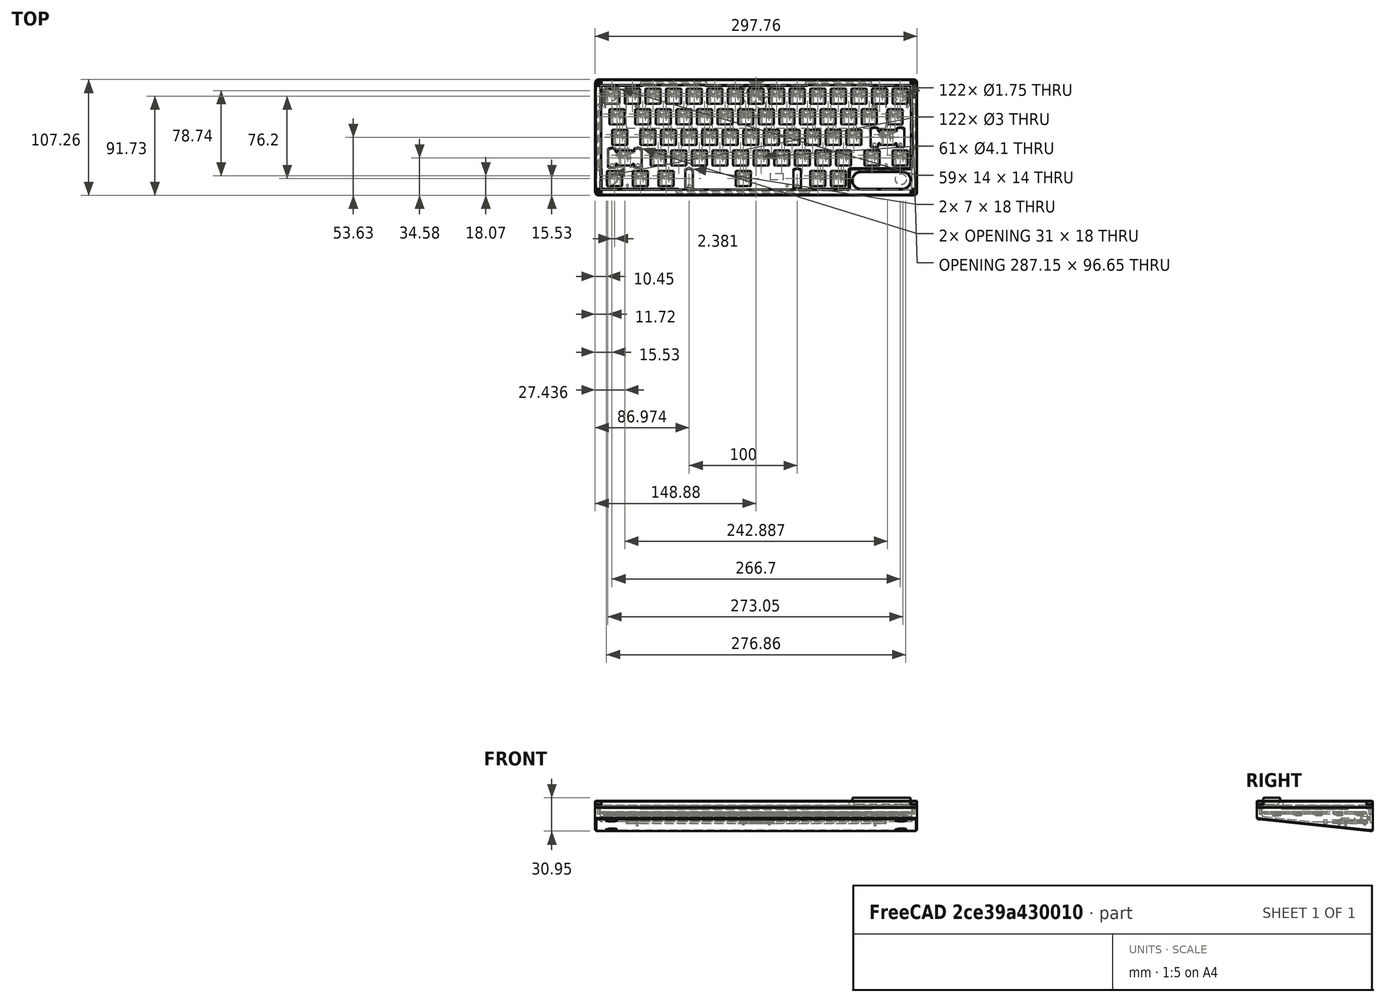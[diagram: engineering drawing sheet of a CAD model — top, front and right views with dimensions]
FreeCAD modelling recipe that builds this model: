
FCSTD DOCUMENT  (FreeCAD 0.20R29603 (Git))
Label: Five_Octave_Enclosure
License: All rights reserved
LicenseURL: http://en.wikipedia.org/wiki/All_rights_reserved
objects: Sketcher::SketchObject×21, PartDesign::Pocket×11, TechDraw::DrawViewBalloon×10, PartDesign::Fillet×9, PartDesign::Pad×6, PartDesign::Body×6, PartDesign::Chamfer×5, PartDesign::Hole×4, Part::Feature×3, PartDesign::Boolean×2, Part::MultiFuse×1, App::DocumentObjectGroup×1, TechDraw::DrawSVGTemplate×1, TechDraw::DrawViewPart×1, TechDraw::DrawPage×1
note: 103 computed .brp shape members not serialized (recipe doc carries the construction recipe); baked Part::Feature solids carry a one-line shape summary decoded from their .brp

FEATURE [Part::Feature] Feature  label="Five_Octave_MCU"
  shape: bbox 28.58 x 28.58 x 3.65 mm, 932 faces, 28 solids (baked)
FEATURE [Sketcher::SketchObject] Sketch
  AttachmentOffset = pos=(0,0,1.65) rot=(0,0,1;0rad)
  FullyConstrained = true
  MapMode = 5
  Placement = pos=(0,0,1.65) rot=(0,0,1;0rad)
  Support = -> [XY_Plane]
  expr: Constraints[12] = 15.637mm
  sketch-geometry (5):
    g0: LineSegment StartX=-4.47 StartY=15.637 StartZ=0 EndX=4.47 EndY=15.637 EndZ=0
    g1: LineSegment StartX=4.47 StartY=15.637 StartZ=0 EndX=4.47 EndY=8.337 EndZ=0
    g2: LineSegment StartX=4.47 StartY=8.337 StartZ=0 EndX=-4.47 EndY=8.337 EndZ=0
    g3: LineSegment StartX=-4.47 StartY=8.337 StartZ=0 EndX=-4.47 EndY=15.637 EndZ=0
    g4: GeomPoint X=0 Y=15.637 Z=0
  constraints (13):
    c: Coincident(g0,g1)
    c: Coincident(g1,g2)
    c: Coincident(g2,g3)
    c: Coincident(g3,g0)
    c: Horizontal(g0)
    c: Horizontal(g2)
    c: Vertical(g1)
    c: Vertical(g3)
    c: DistanceX(g0,g0) = 8.94
    c: DistanceY(g1,g1) = 7.3
    c: Symmetric(g0,g0,g4)
    c: PointOnObject(g4,g-2)
    c: DistanceY(g-1,g4) = 15.637
FEATURE [PartDesign::Pad] Pad
  Direction = (0,0,1)
  Length = 3.2
  Length2 = 10
  Profile = -> Sketch
  ReferenceAxis = -> Sketch [N_Axis]
  Type = 0
FEATURE [Sketcher::SketchObject] Sketch001
  ExternalGeometry = -> [Pad]
  FullyConstrained = true
  MapMode = 5
  Placement = pos=(0,15.637,0) rot=(0,0.707107,0.707107;3.14159rad)
  Support = -> [Pad]
  sketch-geometry (12):
    g0: ArcOfCircle CenterX=-3.22 CenterY=3.6 CenterZ=0 NormalX=0 NormalY=0 NormalZ=1 AngleXU=0 Radius=1.25 StartAngle=1.5708 EndAngle=3.14159
    g1: LineSegment StartX=-4.47 StartY=4.85 StartZ=0 EndX=-3.22 EndY=4.85 EndZ=0
    g2: LineSegment StartX=-4.47 StartY=3.6 StartZ=0 EndX=-4.47 EndY=4.85 EndZ=0
    g3: ArcOfCircle CenterX=3.22 CenterY=3.6 CenterZ=0 NormalX=0 NormalY=0 NormalZ=1 AngleXU=0 Radius=1.25 StartAngle=1e-16 EndAngle=1.5708
    g4: LineSegment StartX=3.22 StartY=4.85 StartZ=0 EndX=4.47 EndY=4.85 EndZ=0
    g5: LineSegment StartX=4.47 StartY=3.6 StartZ=0 EndX=4.47 EndY=4.85 EndZ=0
    g6: ArcOfCircle CenterX=-3.22 CenterY=2.9 CenterZ=0 NormalX=0 NormalY=0 NormalZ=1 AngleXU=0 Radius=1.25 StartAngle=3.14159 EndAngle=4.71239
    g7: LineSegment StartX=-4.47 StartY=1.65 StartZ=0 EndX=-4.47 EndY=2.9 EndZ=0
    g8: LineSegment StartX=-4.47 StartY=1.65 StartZ=0 EndX=-3.22 EndY=1.65 EndZ=0
    g9: ArcOfCircle CenterX=3.22 CenterY=2.9 CenterZ=0 NormalX=0 NormalY=0 NormalZ=1 AngleXU=0 Radius=1.25 StartAngle=4.71239 EndAngle=6.28319
    g10: LineSegment StartX=4.47 StartY=1.65 StartZ=0 EndX=3.22 EndY=1.65 EndZ=0
    g11: LineSegment StartX=4.47 StartY=1.65 StartZ=0 EndX=4.47 EndY=2.9 EndZ=0
  constraints (36):
    c: PointOnObject(g0,g-3)
    c: PointOnObject(g0,g-5)
    c: Radius(g0) = 1.25
    c: Coincident(g1,g-5)
    c: Coincident(g1,g0)
    c: DistanceX(g1,g1) = 1.25
    c: Coincident(g2,g0)
    c: Coincident(g2,g1)
    c: DistanceY(g2,g2) = 1.25
    c: PointOnObject(g3,g-3)
    c: PointOnObject(g3,g-6)
    c: Coincident(g4,g3)
    c: Coincident(g4,g-6)
    c: Coincident(g5,g4)
    c: Coincident(g5,g3)
    c: PointOnObject(g6,g-5)
    c: PointOnObject(g6,g-4)
    c: Equal(g6,g0)
    c: Equal(g3,g0)
    c: Equal(g1,g4)
    c: Equal(g5,g2)
    c: Coincident(g7,g-5)
    c: Coincident(g8,g7)
    c: Coincident(g8,g6)
    c: Coincident(g6,g7)
    c: Equal(g7,g2)
    c: Equal(g1,g8)
    c: PointOnObject(g9,g-6)
    c: PointOnObject(g9,g-4)
    c: Equal(g9,g0)
    c: Coincident(g10,g-6)
    c: Coincident(g11,g10)
    c: Coincident(g9,g11)
    c: Coincident(g10,g9)
    c: Equal(g10,g1)
    c: Equal(g11,g2)
FEATURE [PartDesign::Pocket] Pocket
  BaseFeature = -> Pad
  Direction = (0,-1,2e-16)
  Length = 7.3
  Length2 = 5
  Profile = -> Sketch001
  ReferenceAxis = -> Sketch001 [N_Axis]
  Type = 0
FEATURE [PartDesign::Body] Body  label="USB"
  Group = -> [Sketch,Pad,Sketch001,Pocket]
  Origin = -> Origin
  Tip = -> Pocket
FEATURE [Part::MultiFuse] Fusion  label="MCU"
  Placement = pos=(0,34.1625,0) rot=(0,0,1;0rad)
  Shapes = -> [Body,Feature]
  expr: .Placement.Base.y = 19.05mm * (5 - 1.5) / 2 + 1mm - 0.35mm / 2
FEATURE [Part::Feature] Feature001  label="Five_Octave_Keys"
  Placement = pos=(0,0,9.2) rot=(0,1,0;3.14159rad)
  shape: bbox 285.8 x 95.25 x 3.65 mm, 9961 faces, 246 solids (baked)
  expr: .Placement.Base.z = 3.2mm + 6mm
FEATURE [Part::Feature] Solid  label="Five_Octave_Plate"
  Placement = pos=(0,0,12.6) rot=(0,0,1;0rad)
  shape: bbox 290.8 x 100.3 x 1.6 mm, 520 faces (baked)
  expr: .Placement.Base.z = 3.2mm + 1.85mm + 3.2mm + 0.1mm + 0.85mm + 3.4mm
FEATURE [App::DocumentObjectGroup] Group  label="External Components"
  Group = -> [Fusion,Feature001,Solid]
FEATURE [Sketcher::SketchObject] Sketch002
  AttachmentOffset = pos=(0,0,-20) rot=(0,0,1;0rad)
  FullyConstrained = true
  MapMode = 5
  Placement = pos=(0,0,-20) rot=(0,0,1;0rad)
  Support = -> [XY_Plane001]
  expr: Constraints[10] = 19.05mm * 5
  expr: Constraints[19] = 5mm + 1mm
  expr: Constraints[20] = 5mm + 1mm
  expr: Constraints[9] = 19.05mm * 15
  sketch-geometry (8):
    g0: LineSegment StartX=-142.875 StartY=47.625 StartZ=0 EndX=142.875 EndY=47.625 EndZ=0
    g1: LineSegment StartX=142.875 StartY=47.625 StartZ=0 EndX=142.875 EndY=-47.625 EndZ=0
    g2: LineSegment StartX=142.875 StartY=-47.625 StartZ=0 EndX=-142.875 EndY=-47.625 EndZ=0
    g3: LineSegment StartX=-142.875 StartY=-47.625 StartZ=0 EndX=-142.875 EndY=47.625 EndZ=0
    g4: LineSegment StartX=-148.875 StartY=53.625 StartZ=0 EndX=148.875 EndY=53.625 EndZ=0
    g5: LineSegment StartX=148.875 StartY=53.625 StartZ=0 EndX=148.875 EndY=-53.625 EndZ=0
    g6: LineSegment StartX=148.875 StartY=-53.625 StartZ=0 EndX=-148.875 EndY=-53.625 EndZ=0
    g7: LineSegment StartX=-148.875 StartY=-53.625 StartZ=0 EndX=-148.875 EndY=53.625 EndZ=0
  constraints (22):
    c: Coincident(g0,g1)
    c: Coincident(g1,g2)
    c: Coincident(g2,g3)
    c: Coincident(g3,g0)
    c: Horizontal(g0)
    c: Horizontal(g2)
    c: Vertical(g1)
    c: Vertical(g3)
    c: Symmetric(g0,g1,g-1)
    c: DistanceX(g0,g0) = 285.75
    c: DistanceY(g3,g3) = 95.25
    c: Coincident(g4,g5)
    c: Coincident(g5,g6)
    c: Coincident(g6,g7)
    c: Coincident(g7,g4)
    c: Horizontal(g4)
    c: Horizontal(g6)
    c: Vertical(g5)
    c: Vertical(g7)
    c: DistanceX(g4,g0) = 6
    c: DistanceY(g0,g4) = 6
    c: Symmetric(g4,g5,g-1)
FEATURE [PartDesign::Pad] Pad001
  Direction = (0,0,1)
  Length = 33.4
  Length2 = 10
  Profile = -> Sketch002
  ReferenceAxis = -> Sketch002 [N_Axis]
  Type = 0
  expr: Length = 12.6mm + 1.6mm / 2 + 20mm
FEATURE [Sketcher::SketchObject] Sketch003
  ExternalGeometry = -> [Pad001]
  FullyConstrained = true
  MapMode = 5
  Placement = pos=(148.875,0,0) rot=(0.57735,0.57735,0.57735;2.0944rad)
  Support = -> [Pad001]
  sketch-geometry (5):
    g0: LineSegment StartX=-53.625 StartY=2.61969 StartZ=0 EndX=53.625 EndY=-8.65274 EndZ=0
    g1: LineSegment StartX=53.625 StartY=-20 StartZ=0 EndX=-53.625 EndY=-20 EndZ=0
    g2: LineSegment StartX=-53.625 StartY=-20 StartZ=0 EndX=-53.625 EndY=2.61969 EndZ=0
    g3: LineSegment StartX=53.625 StartY=-20 StartZ=0 EndX=53.625 EndY=-8.65274 EndZ=0
    g4: LineSegment StartX=0 StartY=0 StartZ=0 EndX=-0.313585 EndY=-2.98357 EndZ=0
  constraints (13):
    c: PointOnObject(g0,g-3)
    c: Coincident(g3,g-4)
    c: Coincident(g1,g3)
    c: Coincident(g1,g-3)
    c: Coincident(g2,g1)
    c: Coincident(g2,g0)
    c: Angle(g0,g-1) = 0.10472
    c: Coincident(g3,g0)
    c: PointOnObject(g0,g-4)
    c: Coincident(g4,g-1)
    c: PointOnObject(g4,g0)
    c: Perpendicular(g0,g4)
    c: Distance(g4) = 3
FEATURE [PartDesign::Pocket] Pocket001
  BaseFeature = -> Pad001
  Direction = (-1,0,0)
  Length = 310
  Length2 = 5
  Profile = -> Sketch003
  ReferenceAxis = -> Sketch003 [N_Axis]
  Type = 0
FEATURE [Sketcher::SketchObject] Sketch004
  AttachmentOffset = pos=(0,0,-20) rot=(0,0,1;0rad)
  FullyConstrained = true
  MapMode = 5
  Placement = pos=(0,0,-20) rot=(0,0,1;0rad)
  Support = -> [XY_Plane002]
  expr: .AttachmentOffset.Base.z = -20mm
  expr: Constraints[10] = 19.05mm * 15
  expr: Constraints[11] = 19.05mm * 5
  sketch-geometry (10):
    g0: LineSegment StartX=142.875 StartY=-47.625 StartZ=0 EndX=142.875 EndY=47.625 EndZ=0
    g1: LineSegment StartX=142.875 StartY=47.625 StartZ=0 EndX=-142.875 EndY=47.625 EndZ=0
    g2: LineSegment StartX=-142.875 StartY=47.625 StartZ=0 EndX=-142.875 EndY=-47.625 EndZ=0
    g3: LineSegment StartX=-142.875 StartY=-47.625 StartZ=0 EndX=142.875 EndY=-47.625 EndZ=0
    g4: GeomPoint X=0 Y=0 Z=0
    g5: LineSegment StartX=143.875 StartY=-48.625 StartZ=0 EndX=143.875 EndY=48.625 EndZ=0
    g6: LineSegment StartX=143.875 StartY=48.625 StartZ=0 EndX=-143.875 EndY=48.625 EndZ=0
    g7: LineSegment StartX=-143.875 StartY=48.625 StartZ=0 EndX=-143.875 EndY=-48.625 EndZ=0
    g8: LineSegment StartX=-143.875 StartY=-48.625 StartZ=0 EndX=143.875 EndY=-48.625 EndZ=0
    g9: GeomPoint X=0 Y=0 Z=0
  constraints (24):
    c: Coincident(g0,g1)
    c: Coincident(g1,g2)
    c: Coincident(g2,g3)
    c: Coincident(g3,g0)
    c: Horizontal(g1)
    c: Horizontal(g3)
    c: Vertical(g0)
    c: Vertical(g2)
    c: Symmetric(g1,g0,g4)
    c: Coincident(g4,g-1)
    c: DistanceX(g1,g1) = 285.75
    c: DistanceY(g2,g2) = 95.25
    c: Coincident(g5,g6)
    c: Coincident(g6,g7)
    c: Coincident(g7,g8)
    c: Coincident(g8,g5)
    c: Horizontal(g6)
    c: Horizontal(g8)
    c: Vertical(g5)
    c: Vertical(g7)
    c: Symmetric(g6,g5,g9)
    c: Coincident(g9,g4)
    c: DistanceX(g6,g1) = 1
    c: DistanceY(g1,g6) = 1
FEATURE [PartDesign::Pad] Pad002
  Direction = (0,0,1)
  Length = 33.4
  Length2 = 10
  Profile = -> Sketch004
  ReferenceAxis = -> Sketch004 [N_Axis]
  Type = 0
  expr: Length = 12.6mm + 1.6mm / 2 + 20mm
FEATURE [Sketcher::SketchObject] Sketch005
  ExternalGeometry = -> [Pad002]
  FullyConstrained = true
  MapMode = 5
  Placement = pos=(143.875,0,0) rot=(0.57735,0.57735,0.57735;2.0944rad)
  Support = -> [Pad002]
  sketch-geometry (6):
    g0: LineSegment StartX=-48.625 StartY=-20 StartZ=0 EndX=48.625 EndY=-20 EndZ=0
    g1: LineSegment StartX=-48.625 StartY=5.11069 StartZ=0 EndX=0 EndY=0 EndZ=0
    g2: LineSegment StartX=-48.625 StartY=5.11069 StartZ=0 EndX=-48.625 EndY=-20 EndZ=0
    g3: LineSegment StartX=0 StartY=0 StartZ=0 EndX=48.625 EndY=0 EndZ=0
    g4: LineSegment StartX=48.625 StartY=0 StartZ=0 EndX=48.625 EndY=-20 EndZ=0
    g5: LineSegment StartX=0 StartY=0 StartZ=0 EndX=-48.625 EndY=0 EndZ=0
  constraints (15):
    c: Coincident(g0,g-3)
    c: PointOnObject(g1,g-5)
    c: Coincident(g2,g1)
    c: Coincident(g2,g0)
    c: Coincident(g0,g-5)
    c: Coincident(g3,g1)
    c: Horizontal(g3)
    c: Coincident(g4,g3)
    c: Coincident(g4,g0)
    c: Coincident(g-1,g1)
    c: PointOnObject(g3,g-4)
    c: Coincident(g5,g1)
    c: PointOnObject(g5,g2)
    c: Horizontal(g5)
    c: Angle(g1,g5) = 0.10472
FEATURE [PartDesign::Pocket] Pocket002
  BaseFeature = -> Pad002
  Direction = (-1,0,0)
  Length = 300
  Length2 = 5
  Profile = -> Sketch005
  ReferenceAxis = -> Sketch005 [N_Axis]
  Type = 0
FEATURE [PartDesign::Body] Body002  label="Case_Pocket"
  Group = -> [Sketch004,Pad002,Sketch005,Pocket002]
  Origin = -> Origin002
  Tip = -> Pocket002
FEATURE [PartDesign::Boolean] Boolean
  BaseFeature = -> Pocket001
  Group = -> [Body002]
  Type = 1
FEATURE [PartDesign::Fillet] Fillet
  Base = -> Boolean [Edge22,Edge25,Edge19,Edge20]
  BaseFeature = -> Boolean
  Radius = 2
  SupportTransform = false
  UseAllEdges = false
FEATURE [Sketcher::SketchObject] Sketch006
  ExternalGeometry = -> [Fillet]
  FullyConstrained = true
  MapMode = 5
  Placement = pos=(0,0,13.4) rot=(0,0,1;0rad)
  Support = -> [Fillet]
  expr: Constraints[10] = 19.05mm * 2.5 - 2mm
  expr: Constraints[20] = 19.05mm * 3 + 4mm
  expr: Constraints[21] = 19.05mm * 2.5 - 2mm
  expr: Constraints[31] = 19.05mm * 3 + 4mm
  expr: Constraints[32] = 19.05mm * 1.5 + 2mm
  expr: Constraints[42] = 19.05mm * 2 + 4mm
  expr: Constraints[43] = 19.05mm * 1.5 + 2mm
  expr: Constraints[53] = 19.05mm * 6.25 + 4mm
  expr: Constraints[54] = 19.05mm * (7.5 - 1.25 * 3) + 2mm
  expr: Constraints[9] = 19.05mm * 3 + 4mm
  sketch-geometry (20):
    g0: LineSegment StartX=-106.775 StartY=51.625 StartZ=0 EndX=-45.625 EndY=51.625 EndZ=0
    g1: LineSegment StartX=-45.625 StartY=51.625 StartZ=0 EndX=-45.625 EndY=48.625 EndZ=0
    g2: LineSegment StartX=-45.625 StartY=48.625 StartZ=0 EndX=-106.775 EndY=48.625 EndZ=0
    g3: LineSegment StartX=-106.775 StartY=48.625 StartZ=0 EndX=-106.775 EndY=51.625 EndZ=0
    g4: LineSegment StartX=45.625 StartY=51.625 StartZ=0 EndX=106.775 EndY=51.625 EndZ=0
    g5: LineSegment StartX=106.775 StartY=51.625 StartZ=0 EndX=106.775 EndY=48.625 EndZ=0
    g6: LineSegment StartX=106.775 StartY=48.625 StartZ=0 EndX=45.625 EndY=48.625 EndZ=0
    g7: LineSegment StartX=45.625 StartY=48.625 StartZ=0 EndX=45.625 EndY=51.625 EndZ=0
    g8: LineSegment StartX=-146.875 StartY=30.575 StartZ=0 EndX=-143.875 EndY=30.575 EndZ=0
    g9: LineSegment StartX=-143.875 StartY=30.575 StartZ=0 EndX=-143.875 EndY=-30.575 EndZ=0
    g10: LineSegment StartX=-143.875 StartY=-30.575 StartZ=0 EndX=-146.875 EndY=-30.575 EndZ=0
    g11: LineSegment StartX=-146.875 StartY=-30.575 StartZ=0 EndX=-146.875 EndY=30.575 EndZ=0
    g12: LineSegment StartX=143.875 StartY=30.575 StartZ=0 EndX=146.875 EndY=30.575 EndZ=0
    g13: LineSegment StartX=146.875 StartY=30.575 StartZ=0 EndX=146.875 EndY=-11.525 EndZ=0
    g14: LineSegment StartX=146.875 StartY=-11.525 StartZ=0 EndX=143.875 EndY=-11.525 EndZ=0
    g15: LineSegment StartX=143.875 StartY=-11.525 StartZ=0 EndX=143.875 EndY=30.575 EndZ=0
    g16: LineSegment StartX=-73.4375 StartY=-48.625 StartZ=0 EndX=49.625 EndY=-48.625 EndZ=0
    g17: LineSegment StartX=49.625 StartY=-48.625 StartZ=0 EndX=49.625 EndY=-51.625 EndZ=0
    g18: LineSegment StartX=49.625 StartY=-51.625 StartZ=0 EndX=-73.4375 EndY=-51.625 EndZ=0
    g19: LineSegment StartX=-73.4375 StartY=-51.625 StartZ=0 EndX=-73.4375 EndY=-48.625 EndZ=0
  constraints (60):
    c: Coincident(g0,g1)
    c: Coincident(g1,g2)
    c: Coincident(g2,g3)
    c: Coincident(g3,g0)
    c: Horizontal(g0)
    c: Horizontal(g2)
    c: Vertical(g1)
    c: Vertical(g3)
    c: PointOnObject(g1,g-4)
    c: DistanceX(g0,g0) = 61.15
    c: DistanceX(g0,g-1) = 45.625
    c: Coincident(g4,g5)
    c: Coincident(g5,g6)
    c: Coincident(g6,g7)
    c: Coincident(g7,g4)
    c: Horizontal(g4)
    c: Horizontal(g6)
    c: Vertical(g5)
    c: Vertical(g7)
    c: PointOnObject(g5,g-4)
    c: DistanceX(g4,g4) = 61.15
    c: DistanceX(g-1,g4) = 45.625
    c: Coincident(g8,g9)
    c: Coincident(g9,g10)
    c: Coincident(g10,g11)
    c: Coincident(g11,g8)
    c: Horizontal(g8)
    c: Horizontal(g10)
    c: Vertical(g9)
    c: Vertical(g11)
    c: PointOnObject(g9,g-6)
    c: DistanceY(g11,g11) = 61.15
    c: DistanceY(g-1,g8) = 30.575
    c: Coincident(g12,g13)
    c: Coincident(g13,g14)
    c: Coincident(g14,g15)
    c: Coincident(g15,g12)
    c: Horizontal(g12)
    c: Horizontal(g14)
    c: Vertical(g13)
    c: Vertical(g15)
    c: PointOnObject(g12,g-10)
    c: DistanceY(g13,g13) = 42.1
    c: DistanceY(g-1,g12) = 30.575
    c: Coincident(g16,g17)
    c: Coincident(g17,g18)
    c: Coincident(g18,g19)
    c: Coincident(g19,g16)
    c: Horizontal(g16)
    c: Horizontal(g18)
    c: Vertical(g17)
    c: Vertical(g19)
    c: PointOnObject(g16,g-8)
    c: DistanceX(g18,g18) = 123.062
    c: DistanceX(g18,g-1) = 73.4375
    c: DistanceY(g3,g3) = 3
    c: DistanceY(g17,g17) = 3
    c: DistanceX(g14,g14) = 3
    c: DistanceY(g7,g7) = 3
    c: DistanceX(g8,g8) = 3
FEATURE [PartDesign::Pocket] Pocket003  label="Pocket003 - Poron"
  BaseFeature = -> Fillet
  Direction = (0,0,-1)
  Length = 1.6
  Length2 = 5
  Profile = -> Sketch006
  ReferenceAxis = -> Sketch006 [N_Axis]
  Type = 0
FEATURE [PartDesign::Fillet] Fillet001
  Base = -> Pocket003 [Edge70,Edge68,Edge65,Edge63,Edge50,Edge48,Edge95,Edge93,Edge83,Edge81]
  BaseFeature = -> Pocket003
  Radius = 2
  SupportTransform = false
  UseAllEdges = false
FEATURE [Sketcher::SketchObject] Sketch007
  ExternalGeometry = -> [Fillet001]
  FullyConstrained = true
  MapMode = 5
  Support = -> [Fillet001]
  expr: Constraints[18] = 19.05mm * 1.5
  expr: Constraints[19] = 19.05mm * 1.5
  expr: Constraints[20] = 19.05mm * 1.5 / 2
  sketch-geometry (41):
    g0: LineSegment StartX=120.2 StartY=48.625 StartZ=0 EndX=120.2 EndY=8.225 EndZ=0
    g1: LineSegment StartX=120.2 StartY=8.225 StartZ=0 EndX=-120.2 EndY=8.225 EndZ=0
    g2: LineSegment StartX=-120.2 StartY=8.225 StartZ=0 EndX=-120.2 EndY=48.625 EndZ=0
    g3: LineSegment StartX=-14.2875 StartY=48.625 StartZ=0 EndX=14.2875 EndY=48.625 EndZ=0
    g4: LineSegment StartX=14.2875 StartY=48.625 StartZ=0 EndX=14.2875 EndY=20.05 EndZ=0
    g5: LineSegment StartX=14.2875 StartY=20.05 StartZ=0 EndX=-14.2875 EndY=20.05 EndZ=0
    g6: LineSegment StartX=-14.2875 StartY=20.05 StartZ=0 EndX=-14.2875 EndY=48.625 EndZ=0
    g7: LineSegment StartX=-12 StartY=46.3375 StartZ=0 EndX=12 EndY=46.3375 EndZ=0
    g8: LineSegment StartX=12 StartY=46.3375 StartZ=0 EndX=12 EndY=22.3375 EndZ=0
    g9: LineSegment StartX=12 StartY=22.3375 StartZ=0 EndX=-12 EndY=22.3375 EndZ=0
    g10: LineSegment StartX=-12 StartY=22.3375 StartZ=0 EndX=-12 EndY=46.3375 EndZ=0
    g11: GeomPoint X=-2e-15 Y=34.3375 Z=0
    g12: LineSegment StartX=-9.7125 StartY=44.05 StartZ=0 EndX=-9.7125 EndY=48.625 EndZ=0
    g13: LineSegment StartX=-9.7125 StartY=48.625 StartZ=0 EndX=-14.2875 EndY=48.625 EndZ=0
    g14: LineSegment StartX=-14.2875 StartY=48.625 StartZ=0 EndX=-14.2875 EndY=44.05 EndZ=0
    g15: LineSegment StartX=-14.2875 StartY=44.05 StartZ=0 EndX=-9.7125 EndY=44.05 EndZ=0
    g16: GeomPoint X=-12 Y=46.3375 Z=0
    g17: LineSegment StartX=9.7125 StartY=44.05 StartZ=0 EndX=9.7125 EndY=48.625 EndZ=0
    g18: LineSegment StartX=9.7125 StartY=48.625 StartZ=0 EndX=14.2875 EndY=48.625 EndZ=0
    g19: LineSegment StartX=14.2875 StartY=48.625 StartZ=0 EndX=14.2875 EndY=44.05 EndZ=0
    g20: LineSegment StartX=14.2875 StartY=44.05 StartZ=0 EndX=9.7125 EndY=44.05 EndZ=0
    g21: GeomPoint X=12 Y=46.3375 Z=0
    g22: LineSegment StartX=9.7125 StartY=24.625 StartZ=0 EndX=9.7125 EndY=20.05 EndZ=0
    g23: LineSegment StartX=9.7125 StartY=20.05 StartZ=0 EndX=14.2875 EndY=20.05 EndZ=0
    g24: LineSegment StartX=14.2875 StartY=20.05 StartZ=0 EndX=14.2875 EndY=24.625 EndZ=0
    g25: LineSegment StartX=14.2875 StartY=24.625 StartZ=0 EndX=9.7125 EndY=24.625 EndZ=0
    g26: GeomPoint X=12 Y=22.3375 Z=0
    g27: LineSegment StartX=-9.7125 StartY=24.625 StartZ=0 EndX=-9.7125 EndY=20.05 EndZ=0
    g28: LineSegment StartX=-9.7125 StartY=20.05 StartZ=0 EndX=-14.2875 EndY=20.05 EndZ=0
    g29: LineSegment StartX=-14.2875 StartY=20.05 StartZ=0 EndX=-14.2875 EndY=24.625 EndZ=0
    g30: LineSegment StartX=-14.2875 StartY=24.625 StartZ=0 EndX=-9.7125 EndY=24.625 EndZ=0
    g31: GeomPoint X=-12 Y=22.3375 Z=0
    g32: LineSegment StartX=14.2875 StartY=48.625 StartZ=0 EndX=120.2 EndY=48.625 EndZ=0
    g33: LineSegment StartX=14.2875 StartY=44.05 StartZ=0 EndX=14.2875 EndY=48.625 EndZ=0
    g34: LineSegment StartX=9.7125 StartY=44.05 StartZ=0 EndX=14.2875 EndY=44.05 EndZ=0
    g35: LineSegment StartX=9.7125 StartY=48.625 StartZ=0 EndX=9.7125 EndY=44.05 EndZ=0
    g36: LineSegment StartX=-120.2 StartY=48.625 StartZ=0 EndX=-14.2875 EndY=48.625 EndZ=0
    g37: LineSegment StartX=-14.2875 StartY=48.625 StartZ=0 EndX=-14.2875 EndY=44.05 EndZ=0
    g38: LineSegment StartX=-14.2875 StartY=44.05 StartZ=0 EndX=-9.7125 EndY=44.05 EndZ=0
    g39: LineSegment StartX=-9.7125 StartY=44.05 StartZ=0 EndX=-9.7125 EndY=48.625 EndZ=0
    g40: LineSegment StartX=-9.7125 StartY=48.625 StartZ=0 EndX=9.7125 EndY=48.625 EndZ=0
  constraints (97):
    c: Coincident(g32,g0)
    c: Coincident(g0,g1)
    c: Coincident(g1,g2)
    c: Coincident(g2,g36)
    c: Horizontal(g1)
    c: Vertical(g0)
    c: Vertical(g2)
    c: DistanceX(g1,g1) = 240.4
    c: DistanceY(g2,g2) = 40.4
    c: DistanceX(g1,g-1) = 120.2
    c: Coincident(g3,g4)
    c: Coincident(g4,g5)
    c: Coincident(g5,g6)
    c: Coincident(g6,g3)
    c: Horizontal(g3)
    c: Horizontal(g5)
    c: Vertical(g4)
    c: Vertical(g6)
    c: DistanceX(g3,g3) = 28.575
    c: DistanceY(g6,g6) = 28.575
    c: DistanceX(g5,g-1) = 14.2875
    c: Coincident(g7,g8)
    c: Coincident(g8,g9)
    c: Coincident(g9,g10)
    c: Coincident(g10,g7)
    c: Horizontal(g7)
    c: Horizontal(g9)
    c: Vertical(g8)
    c: Vertical(g10)
    c: DistanceY(g10,g10) = 24
    c: DistanceX(g7,g7) = 24
    c: Symmetric(g3,g4,g11)
    c: Symmetric(g7,g8,g11)
    c: Coincident(g12,g13)
    c: Coincident(g13,g14)
    c: Coincident(g14,g15)
    c: Coincident(g15,g12)
    c: Horizontal(g13)
    c: Horizontal(g15)
    c: Vertical(g12)
    c: Vertical(g14)
    c: Symmetric(g13,g12,g16)
    c: Coincident(g16,g7)
    c: Coincident(g13,g3)
    c: Coincident(g17,g18)
    c: Coincident(g18,g19)
    c: Coincident(g19,g20)
    c: Coincident(g20,g17)
    c: Horizontal(g18)
    c: Horizontal(g20)
    c: Vertical(g17)
    c: Vertical(g19)
    c: Symmetric(g18,g17,g21)
    c: Coincident(g21,g7)
    c: Coincident(g18,g3)
    c: Coincident(g22,g23)
    c: Coincident(g23,g24)
    c: Coincident(g24,g25)
    c: Coincident(g25,g22)
    c: Horizontal(g23)
    c: Horizontal(g25)
    c: Vertical(g22)
    c: Vertical(g24)
    c: Symmetric(g23,g22,g26)
    c: Coincident(g26,g8)
    c: Coincident(g23,g4)
    c: Coincident(g27,g28)
    c: Coincident(g28,g29)
    c: Coincident(g29,g30)
    c: Coincident(g30,g27)
    c: Horizontal(g28)
    c: Horizontal(g30)
    c: Vertical(g27)
    c: Vertical(g29)
    c: Symmetric(g28,g27,g31)
    c: Coincident(g31,g9)
    c: Coincident(g28,g5)
    c: Coincident(g33,g32)
    c: Horizontal(g32)
    c: Coincident(g34,g33)
    c: Coincident(g35,g34)
    c: Coincident(g40,g35)
    c: Coincident(g3,g32)
    c: Coincident(g19,g33)
    c: Coincident(g17,g34)
    c: Coincident(g37,g38)
    c: Coincident(g36,g37)
    c: Horizontal(g36)
    c: PointOnObject(g3,g36)
    c: Coincident(g38,g39)
    c: Coincident(g39,g40)
    c: Coincident(g37,g14)
    c: Coincident(g12,g38)
    c: Coincident(g17,g35)
    c: Coincident(g39,g12)
    c: Vertical(g37)
    c: PointOnObject(g2,g-4)
FEATURE [PartDesign::Pocket] Pocket004  label="Pocket004 - MCU margin"
  BaseFeature = -> Fillet001
  Direction = (0,0,-1)
  Length = 1.4
  Length2 = 5
  Profile = -> Sketch007
  ReferenceAxis = -> Sketch007 [N_Axis]
  Type = 0
FEATURE [PartDesign::Fillet] Fillet003
  Base = -> Pocket004 [Edge151,Edge156,Edge154,Edge140,Edge139,Edge146,Edge152,Edge145,Edge176,Edge175,Edge174,Edge159,Edge182,Edge180,Edge178,Edge186,Edge188,Edge190,Edge177,Edge185]
  BaseFeature = -> Pocket004
  Radius = 2
  SupportTransform = false
  UseAllEdges = false
FEATURE [Sketcher::SketchObject] Sketch008
  ExternalGeometry = -> [Fillet003]
  FullyConstrained = true
  MapMode = 5
  Support = -> [Fillet003]
  sketch-geometry (4):
    g0: Circle CenterX=-12 CenterY=46.3375 CenterZ=0 NormalX=0 NormalY=0 NormalZ=1 AngleXU=0 Radius=0.8
    g1: Circle CenterX=-12 CenterY=22.3375 CenterZ=0 NormalX=0 NormalY=0 NormalZ=1 AngleXU=0 Radius=0.8
    g2: Circle CenterX=12 CenterY=22.3375 CenterZ=0 NormalX=0 NormalY=0 NormalZ=1 AngleXU=0 Radius=0.8
    g3: Circle CenterX=12 CenterY=46.3375 CenterZ=0 NormalX=0 NormalY=0 NormalZ=1 AngleXU=0 Radius=0.8
  constraints (12):
    c: Diameter(g0) = 1.6
    c: Vertical(g0,g1)
    c: Horizontal(g1,g2)
    c: Vertical(g2,g3)
    c: Horizontal(g0,g3)
    c: Equal(g0,g3)
    c: Equal(g0,g1)
    c: Equal(g2,g0)
    c: DistanceX(g0,g3) = 24
    c: DistanceY(g1,g0) = 24
    c: DistanceX(g0,g-1) = 12
    c: DistanceY(g0,g-3) = 2.2875
FEATURE [PartDesign::Hole] Hole  label="Hole - MCU screw"
  BaseFeature = -> Fillet003
  CustomThreadClearance = 0
  Depth = 2.6
  DepthType = 0
  Diameter = 1.6
  DrillForDepth = false
  DrillPoint = 1
  DrillPointAngle = 118
  HoleCutCountersinkAngle = 90
  HoleCutCustomValues = false
  HoleCutDepth = 0
  HoleCutDiameter = 6.1
  HoleCutType = 0
  ModelThread = false
  Profile = -> Sketch008
  Tapered = false
  TaperedAngle = 90
  ThreadClass = 0
  ThreadDepth = 2.6
  ThreadDepthType = 0
  ThreadDirection = 0
  ThreadFit = 0
  ThreadSize = 6
  ThreadType = 1
  Threaded = true
  UseCustomThreadClearance = false
FEATURE [Sketcher::SketchObject] Sketch009
  FullyConstrained = true
  MapMode = 5
  Placement = pos=(0,48.625,0) rot=(1,0,0;1.5708rad)
  Support = -> [Hole]
  expr: Constraints[2] = 1.6mm + 3.2mm / 2 + 0.05mm
  sketch-geometry (14):
    g0: LineSegment StartX=0 StartY=0 StartZ=0 EndX=0 EndY=3.25 EndZ=0
    g1: LineSegment StartX=4.545 StartY=2.875 StartZ=0 EndX=4.545 EndY=3.625 EndZ=0
    g2: LineSegment StartX=3.245 StartY=4.925 StartZ=0 EndX=-3.245 EndY=4.925 EndZ=0
    g3: LineSegment StartX=-4.545 StartY=3.625 StartZ=0 EndX=-4.545 EndY=2.875 EndZ=0
    g4: LineSegment StartX=-3.245 StartY=1.575 StartZ=0 EndX=3.245 EndY=1.575 EndZ=0
    g5: GeomPoint X=0 Y=3.25 Z=0
    g6: ArcOfCircle CenterX=-3.245 CenterY=3.625 CenterZ=0 NormalX=0 NormalY=0 NormalZ=1 AngleXU=0 Radius=1.3 StartAngle=1.5708 EndAngle=3.14159
    g7: GeomPoint X=-4.545 Y=4.925 Z=0
    g8: ArcOfCircle CenterX=-3.245 CenterY=2.875 CenterZ=0 NormalX=0 NormalY=0 NormalZ=1 AngleXU=0 Radius=1.3 StartAngle=3.14159 EndAngle=4.71239
    g9: GeomPoint X=-4.545 Y=1.575 Z=0
    g10: ArcOfCircle CenterX=3.245 CenterY=2.875 CenterZ=0 NormalX=0 NormalY=0 NormalZ=1 AngleXU=0 Radius=1.3 StartAngle=4.71239 EndAngle=6.28319
    g11: GeomPoint X=4.545 Y=1.575 Z=0
    g12: ArcOfCircle CenterX=3.245 CenterY=3.625 CenterZ=0 NormalX=0 NormalY=0 NormalZ=1 AngleXU=0 Radius=1.3 StartAngle=1e-16 EndAngle=1.5708
    g13: GeomPoint X=4.545 Y=4.925 Z=0
  constraints (31):
    c: Coincident(g0,g-1)
    c: Vertical(g0)
    c: DistanceY(g0,g0) = 3.25
    c: Horizontal(g2)
    c: Horizontal(g4)
    c: Vertical(g1)
    c: Vertical(g3)
    c: Symmetric(g7,g11,g5)
    c: Coincident(g5,g0)
    c: DistanceX(g7,g13) = 9.09
    c: DistanceY(g9,g7) = 3.35
    c: PointOnObject(g7,g3)
    c: PointOnObject(g7,g2)
    c: Tangent(g3,g6) = -1.5708
    c: Tangent(g2,g6) = -1.5708
    c: Radius(g6) = 1.3
    c: PointOnObject(g9,g3)
    c: PointOnObject(g9,g4)
    c: Tangent(g3,g8) = -1.5708
    c: Tangent(g4,g8) = -1.5708
    c: PointOnObject(g11,g4)
    c: PointOnObject(g11,g1)
    c: Tangent(g4,g10) = -1.5708
    c: Tangent(g1,g10) = -1.5708
    c: PointOnObject(g13,g2)
    c: PointOnObject(g13,g1)
    c: Tangent(g2,g12) = -1.5708
    c: Tangent(g1,g12) = -1.5708
    c: Equal(g6,g8)
    c: Equal(g6,g12)
    c: Equal(g6,g10)
FEATURE [PartDesign::Pocket] Pocket005  label="Pocket005 - USB"
  BaseFeature = -> Hole
  Direction = (0,1,-2e-16)
  Length = 5
  Length2 = 5
  Profile = -> Sketch009
  ReferenceAxis = -> Sketch009 [N_Axis]
  Type = 0
FEATURE [Sketcher::SketchObject] Sketch011
  AttachmentOffset = pos=(0,0,13.4) rot=(0,0,1;0rad)
  FullyConstrained = true
  MapMode = 5
  Placement = pos=(0,0,13.4) rot=(0,0,1;0rad)
  Support = -> [XY_Plane003]
  expr: .AttachmentOffset.Base.z = 12.6mm + 1.6mm / 2
  expr: Constraints[10] = 19.05mm * 15 + 0.5mm * 2
  expr: Constraints[21] = 5mm + 0.5mm
  expr: Constraints[22] = 5mm + 0.5mm
  expr: Constraints[23] = 19.05mm * 5 + 0.5mm * 2
  expr: Constraints[31] = 19.05mm
  expr: Constraints[32] = 19.05mm * 3
  sketch-geometry (14):
    g0: LineSegment StartX=143.375 StartY=-48.125 StartZ=0 EndX=143.375 EndY=48.125 EndZ=0
    g1: LineSegment StartX=143.375 StartY=48.125 StartZ=0 EndX=-143.375 EndY=48.125 EndZ=0
    g2: LineSegment StartX=-143.375 StartY=48.125 StartZ=0 EndX=-143.375 EndY=-48.125 EndZ=0
    g3: LineSegment StartX=-143.375 StartY=-48.125 StartZ=0 EndX=143.375 EndY=-48.125 EndZ=0
    g4: GeomPoint X=0 Y=0 Z=0
    g5: LineSegment StartX=148.875 StartY=-53.625 StartZ=0 EndX=148.875 EndY=53.625 EndZ=0
    g6: LineSegment StartX=148.875 StartY=53.625 StartZ=0 EndX=-148.875 EndY=53.625 EndZ=0
    g7: LineSegment StartX=-148.875 StartY=53.625 StartZ=0 EndX=-148.875 EndY=-53.625 EndZ=0
    g8: LineSegment StartX=-148.875 StartY=-53.625 StartZ=0 EndX=148.875 EndY=-53.625 EndZ=0
    g9: GeomPoint X=0 Y=0 Z=0
    g10: LineSegment StartX=86.225 StartY=-48.125 StartZ=0 EndX=86.225 EndY=-29.075 EndZ=0
    g11: LineSegment StartX=86.225 StartY=-29.075 StartZ=0 EndX=143.375 EndY=-29.075 EndZ=0
    g12: LineSegment StartX=143.375 StartY=48.125 StartZ=0 EndX=143.375 EndY=-29.075 EndZ=0
    g13: LineSegment StartX=86.225 StartY=-48.125 StartZ=0 EndX=-143.375 EndY=-48.125 EndZ=0
  constraints (35):
    c: Coincident(g0,g1)
    c: Coincident(g1,g2)
    c: Coincident(g2,g3)
    c: Coincident(g3,g0)
    c: Horizontal(g1)
    c: Horizontal(g3)
    c: Vertical(g0)
    c: Vertical(g2)
    c: Symmetric(g1,g0,g4)
    c: Coincident(g4,g-1)
    c: DistanceX(g1,g1) = 286.75
    c: Coincident(g5,g6)
    c: Coincident(g6,g7)
    c: Coincident(g7,g8)
    c: Coincident(g8,g5)
    c: Horizontal(g6)
    c: Horizontal(g8)
    c: Vertical(g5)
    c: Vertical(g7)
    c: Symmetric(g6,g5,g9)
    c: Coincident(g9,g4)
    c: DistanceX(g6,g1) = 5.5
    c: DistanceY(g1,g6) = 5.5
    c: DistanceY(g2,g2) = 96.25
    c: Coincident(g10,g11)
    c: Horizontal(g11)
    c: Vertical(g10)
    c: Coincident(g12,g1)
    c: Coincident(g11,g12)
    c: Coincident(g13,g10)
    c: Coincident(g13,g2)
    c: DistanceY(g10,g10) = 19.05
    c: DistanceX(g11,g11) = 57.15
    c: Vertical(g12)
    c: Horizontal(g13)
FEATURE [PartDesign::Pad] Pad003
  Direction = (0,0,1)
  Length = 6
  Length2 = 10
  Profile = -> Sketch011
  ReferenceAxis = -> Sketch011 [N_Axis]
  Type = 0
FEATURE [Sketcher::SketchObject] Sketch012
  ExternalGeometry = -> [Pad003]
  FullyConstrained = true
  MapMode = 5
  Placement = pos=(0,0,13.4) rot=(1,0,0;3.14159rad)
  Support = -> [Pad003]
  expr: Constraints[12] = 19.05mm * 3 + 4mm
  expr: Constraints[14] = 19.05mm * 1.5 + 2mm
  expr: Constraints[26] = 19.05mm * 3 + 4mm
  expr: Constraints[27] = 19.05mm * 2.5 - 2mm
  expr: Constraints[35] = 19.05mm * 3 + 4mm
  expr: Constraints[36] = 19.05mm * 2.5 - 2mm
  expr: Constraints[54] = 19.05mm * 6.25 + 4mm
  expr: Constraints[55] = 19.05mm * 1.25 * 3 - 2mm
  expr: Constraints[68] = 19.05mm * 2 + 4mm
  expr: Constraints[76] = 19.05mm - 2mm
  sketch-geometry (26):
    g0: LineSegment StartX=87.225 StartY=49.125 StartZ=0 EndX=87.225 EndY=30.075 EndZ=0
    g1: LineSegment StartX=87.225 StartY=30.075 StartZ=0 EndX=144.375 EndY=30.075 EndZ=0
    g2: LineSegment StartX=-144.375 StartY=30.575 StartZ=0 EndX=-147.375 EndY=30.575 EndZ=0
    g3: LineSegment StartX=-147.375 StartY=30.575 StartZ=0 EndX=-147.375 EndY=-30.575 EndZ=0
    g4: LineSegment StartX=-144.375 StartY=30.575 StartZ=0 EndX=-144.375 EndY=49.125 EndZ=0
    g5: LineSegment StartX=-144.375 StartY=-30.575 StartZ=0 EndX=-144.375 EndY=-49.125 EndZ=0
    g6: LineSegment StartX=-45.625 StartY=-49.125 StartZ=0 EndX=-45.625 EndY=-52.125 EndZ=0
    g7: LineSegment StartX=-45.625 StartY=-52.125 StartZ=0 EndX=-106.775 EndY=-52.125 EndZ=0
    g8: LineSegment StartX=-106.775 StartY=-52.125 StartZ=0 EndX=-106.775 EndY=-49.125 EndZ=0
    g9: LineSegment StartX=-144.375 StartY=-49.125 StartZ=0 EndX=-106.775 EndY=-49.125 EndZ=0
    g10: LineSegment StartX=106.775 StartY=-49.125 StartZ=0 EndX=106.775 EndY=-52.125 EndZ=0
    g11: LineSegment StartX=106.775 StartY=-52.125 StartZ=0 EndX=45.625 EndY=-52.125 EndZ=0
    g12: LineSegment StartX=45.625 StartY=-52.125 StartZ=0 EndX=45.625 EndY=-49.125 EndZ=0
    g13: LineSegment StartX=-147.375 StartY=-30.575 StartZ=0 EndX=-144.375 EndY=-30.575 EndZ=0
    g14: LineSegment StartX=-45.625 StartY=-49.125 StartZ=0 EndX=45.625 EndY=-49.125 EndZ=0
    g15: LineSegment StartX=106.775 StartY=-49.125 StartZ=0 EndX=144.375 EndY=-49.125 EndZ=0
    g16: LineSegment StartX=49.125 StartY=49.125 StartZ=0 EndX=49.125 EndY=52.125 EndZ=0
    g17: LineSegment StartX=49.125 StartY=52.125 StartZ=0 EndX=-73.9375 EndY=52.125 EndZ=0
    g18: LineSegment StartX=-73.9375 StartY=52.125 StartZ=0 EndX=-73.9375 EndY=49.125 EndZ=0
    g19: LineSegment StartX=-73.9375 StartY=49.125 StartZ=0 EndX=-144.375 EndY=49.125 EndZ=0
    g20: LineSegment StartX=49.125 StartY=49.125 StartZ=0 EndX=87.225 EndY=49.125 EndZ=0
    g21: LineSegment StartX=144.375 StartY=-31.075 StartZ=0 EndX=147.375 EndY=-31.075 EndZ=0
    g22: LineSegment StartX=147.375 StartY=-31.075 StartZ=0 EndX=147.375 EndY=11.025 EndZ=0
    g23: LineSegment StartX=147.375 StartY=11.025 StartZ=0 EndX=144.375 EndY=11.025 EndZ=0
    g24: LineSegment StartX=144.375 StartY=-49.125 StartZ=0 EndX=144.375 EndY=-31.075 EndZ=0
    g25: LineSegment StartX=144.375 StartY=30.075 StartZ=0 EndX=144.375 EndY=11.025 EndZ=0
  constraints (78):
    c: Vertical(g0)
    c: Coincident(g1,g0)
    c: Horizontal(g1)
    c: DistanceX(g4,g-4) = 1
    c: DistanceY(g-4,g4) = 1
    c: DistanceX(g-8,g0) = 1
    c: DistanceY(g-7,g1) = 1
    c: DistanceX(g-7,g1) = 1
    c: DistanceY(g15,g-6) = 1
    c: Coincident(g2,g3)
    c: Horizontal(g2)
    c: Vertical(g3)
    c: DistanceY(g3,g3) = 61.15
    c: DistanceX(g2,g2) = 3
    c: DistanceY(g3,g-1) = 30.575
    c: Vertical(g4)
    c: Coincident(g4,g2)
    c: Vertical(g5)
    c: Coincident(g6,g7)
    c: Coincident(g7,g8)
    c: Horizontal(g7)
    c: Vertical(g6)
    c: Vertical(g8)
    c: Coincident(g9,g5)
    c: Coincident(g9,g8)
    c: Horizontal(g9)
    c: DistanceX(g7,g7) = 61.15
    c: DistanceX(g6,g-1) = 45.625
    c: DistanceY(g8,g8) = 3
    c: DistanceY(g5,g-5) = 1
    c: Coincident(g10,g11)
    c: Coincident(g11,g12)
    c: Horizontal(g11)
    c: Vertical(g10)
    c: Vertical(g12)
    c: DistanceX(g11,g11) = 61.15
    c: DistanceX(g-1,g11) = 45.625
    c: Coincident(g13,g3)
    c: Coincident(g13,g5)
    c: Horizontal(g13)
    c: DistanceX(g5,g-5) = 1
    c: Coincident(g14,g6)
    c: Horizontal(g14)
    c: Coincident(g15,g10)
    c: Horizontal(g15)
    c: Coincident(g14,g12)
    c: DistanceY(g10,g10) = 3
    c: Equal(g8,g6)
    c: Coincident(g16,g17)
    c: Coincident(g17,g18)
    c: Horizontal(g17)
    c: Vertical(g16)
    c: Vertical(g18)
    c: DistanceY(g16,g16) = 3
    c: DistanceX(g17,g17) = 123.062
    c: DistanceX(g-4,g17) = 69.4375
    c: Coincident(g19,g18)
    c: Coincident(g19,g4)
    c: Horizontal(g19)
    c: Coincident(g20,g16)
    c: Coincident(g20,g0)
    c: Horizontal(g20)
    c: DistanceY(g-8,g0) = 1
    c: Coincident(g21,g22)
    c: Coincident(g22,g23)
    c: Horizontal(g21)
    c: Horizontal(g23)
    c: Vertical(g22)
    c: DistanceY(g22,g22) = 42.1
    c: DistanceX(g23,g23) = 3
    c: Coincident(g24,g15)
    c: Coincident(g24,g21)
    c: Vertical(g24)
    c: Coincident(g25,g1)
    c: Coincident(g25,g23)
    c: Vertical(g25)
    c: DistanceY(g-6,g21) = 17.05
    c: DistanceX(g-6,g15) = 1
FEATURE [PartDesign::Pocket] Pocket006  label="Pocket006 - Poron"
  BaseFeature = -> Pad003
  Direction = (0,0,1)
  Length = 1.8
  Length2 = 5
  Profile = -> Sketch012
  ReferenceAxis = -> Sketch012 [N_Axis]
  Type = 0
  expr: Length = 0.8mm + 1mm
FEATURE [PartDesign::Fillet] Fillet005
  Base = -> Pocket006 [Edge64,Edge60,Edge66,Edge72,Edge74,Edge78,Edge82,Edge84,Edge88,Edge92,Edge94,Edge46,Edge48,Edge50,Edge54,Edge56]
  BaseFeature = -> Pocket006
  Radius = 2
  SupportTransform = false
  UseAllEdges = false
FEATURE [PartDesign::Fillet] Fillet006
  Base = -> Fillet005 [Edge155,Edge152,Edge153,Edge156,Edge154,Edge151]
  BaseFeature = -> Fillet005
  Radius = 1
  SupportTransform = false
  UseAllEdges = false
FEATURE [Sketcher::SketchObject] Sketch013
  ExternalGeometry = -> [Fillet006]
  FullyConstrained = true
  MapMode = 5
  Placement = pos=(0,0,19.4) rot=(0,0,1;0rad)
  Support = -> [Fillet006]
  sketch-geometry (4):
    g0: Circle CenterX=-145.875 CenterY=50.625 CenterZ=0 NormalX=0 NormalY=0 NormalZ=1 AngleXU=0 Radius=1.1
    g1: Circle CenterX=145.875 CenterY=50.625 CenterZ=0 NormalX=0 NormalY=0 NormalZ=1 AngleXU=0 Radius=1.1
    g2: Circle CenterX=145.875 CenterY=-50.625 CenterZ=0 NormalX=0 NormalY=0 NormalZ=1 AngleXU=0 Radius=1.1
    g3: Circle CenterX=-145.875 CenterY=-50.625 CenterZ=0 NormalX=0 NormalY=0 NormalZ=1 AngleXU=0 Radius=1.1
  constraints (12):
    c: Diameter(g0) = 2.2
    c: Equal(g0,g1)
    c: Horizontal(g0,g1)
    c: Vertical(g2,g1)
    c: Equal(g2,g0)
    c: Equal(g0,g3)
    c: Vertical(g3,g0)
    c: Horizontal(g3,g2)
    c: DistanceY(g0,g-3) = 3
    c: DistanceX(g-3,g0) = 3
    c: DistanceY(g-4,g3) = 3
    c: DistanceX(g1,g-3) = 3
FEATURE [PartDesign::Pocket] Pocket007  label="Pocket007 - Case screw"
  BaseFeature = -> Fillet006
  Direction = (0,0,-1)
  Length = 10
  Length2 = 5
  Profile = -> Sketch013
  ReferenceAxis = -> Sketch013 [N_Axis]
  Type = 0
FEATURE [Sketcher::SketchObject] Sketch014
  ExternalGeometry = -> [Pocket007]
  FullyConstrained = true
  MapMode = 5
  Placement = pos=(0,0,19.4) rot=(0,0,1;0rad)
  Support = -> [Pocket007]
  sketch-geometry (20):
    g0: ArcOfCircle CenterX=-145.875 CenterY=50.625 CenterZ=0 NormalX=0 NormalY=0 NormalZ=1 AngleXU=0 Radius=2.5 StartAngle=4.71239 EndAngle=6.28319
    g1: LineSegment StartX=-143.375 StartY=50.625 StartZ=0 EndX=-143.375 EndY=53.625 EndZ=0
    g2: LineSegment StartX=-145.875 StartY=48.125 StartZ=0 EndX=-148.875 EndY=48.125 EndZ=0
    g3: LineSegment StartX=-148.875 StartY=48.125 StartZ=0 EndX=-148.875 EndY=53.625 EndZ=0
    g4: LineSegment StartX=-148.875 StartY=53.625 StartZ=0 EndX=-143.375 EndY=53.625 EndZ=0
    g5: ArcOfCircle CenterX=145.875 CenterY=50.625 CenterZ=0 NormalX=0 NormalY=0 NormalZ=1 AngleXU=0 Radius=2.5 StartAngle=3.14159 EndAngle=4.71239
    g6: LineSegment StartX=145.875 StartY=48.125 StartZ=0 EndX=148.875 EndY=48.125 EndZ=0
    g7: LineSegment StartX=143.375 StartY=50.625 StartZ=0 EndX=143.375 EndY=53.625 EndZ=0
    g8: LineSegment StartX=143.375 StartY=53.625 StartZ=0 EndX=148.875 EndY=53.625 EndZ=0
    g9: LineSegment StartX=148.875 StartY=53.625 StartZ=0 EndX=148.875 EndY=48.125 EndZ=0
    g10: ArcOfCircle CenterX=-145.875 CenterY=-50.625 CenterZ=0 NormalX=0 NormalY=0 NormalZ=1 AngleXU=0 Radius=2.5 StartAngle=6.33e-14 EndAngle=1.5708
    g11: LineSegment StartX=-145.875 StartY=-48.125 StartZ=0 EndX=-148.875 EndY=-48.125 EndZ=0
    g12: LineSegment StartX=-143.375 StartY=-50.625 StartZ=0 EndX=-143.375 EndY=-53.625 EndZ=0
    g13: LineSegment StartX=-148.875 StartY=-48.125 StartZ=0 EndX=-148.875 EndY=-53.625 EndZ=0
    g14: LineSegment StartX=-148.875 StartY=-53.625 StartZ=0 EndX=-143.375 EndY=-53.625 EndZ=0
    g15: ArcOfCircle CenterX=145.875 CenterY=-50.625 CenterZ=0 NormalX=0 NormalY=0 NormalZ=1 AngleXU=0 Radius=2.5 StartAngle=1.5708 EndAngle=3.14159
    g16: LineSegment StartX=143.375 StartY=-50.625 StartZ=0 EndX=143.375 EndY=-53.625 EndZ=0
    g17: LineSegment StartX=145.875 StartY=-48.125 StartZ=0 EndX=148.875 EndY=-48.125 EndZ=0
    g18: LineSegment StartX=143.375 StartY=-53.625 StartZ=0 EndX=148.875 EndY=-53.625 EndZ=0
    g19: LineSegment StartX=148.875 StartY=-48.125 StartZ=0 EndX=148.875 EndY=-53.625 EndZ=0
  constraints (56):
    c: Angle(g0) = 1.5708
    c: Radius(g0) = 2.5
    c: Coincident(g1,g0)
    c: Vertical(g1)
    c: Coincident(g2,g0)
    c: Horizontal(g2)
    c: Equal(g2,g1)
    c: Coincident(g3,g2)
    c: Coincident(g4,g3)
    c: Coincident(g4,g1)
    c: Radius(g5) = 2.5
    c: Coincident(g6,g5)
    c: Horizontal(g6)
    c: Coincident(g7,g5)
    c: Vertical(g7)
    c: Equal(g7,g6)
    c: Angle(g5) = 1.5708
    c: Coincident(g8,g7)
    c: Coincident(g9,g8)
    c: Coincident(g9,g6)
    c: Radius(g10) = 2.5
    c: Coincident(g11,g10)
    c: Horizontal(g11)
    c: Coincident(g12,g10)
    c: Vertical(g12)
    c: Angle(g10) = 1.5708
    c: Equal(g11,g12)
    c: Coincident(g13,g11)
    c: Coincident(g14,g13)
    c: Coincident(g14,g12)
    c: Radius(g15) = 2.5
    c: Coincident(g16,g15)
    c: Vertical(g16)
    c: Coincident(g17,g15)
    c: Horizontal(g17)
    c: Equal(g16,g17)
    c: Angle(g15) = 1.5708
    c: Coincident(g18,g16)
    c: Coincident(g19,g17)
    c: Coincident(g19,g18)
    c: Coincident(g3,g-3)
    c: Coincident(g0,g-4)
    c: Horizontal(g4)
    c: Vertical(g3)
    c: Coincident(g-5,g13)
    c: Horizontal(g14)
    c: Vertical(g13)
    c: Coincident(g10,g-6)
    c: Coincident(g5,g-7)
    c: Coincident(g8,g-3)
    c: Horizontal(g8)
    c: Vertical(g9)
    c: Coincident(g18,g-5)
    c: Horizontal(g18)
    c: Vertical(g19)
    c: Coincident(g15,g-8)
FEATURE [PartDesign::Pocket] Pocket008  label="Pocket008 - Case screw"
  BaseFeature = -> Pocket007
  Direction = (0,0,-1)
  Length = 3
  Length2 = 5
  Profile = -> Sketch014
  ReferenceAxis = -> Sketch014 [N_Axis]
  Type = 0
FEATURE [PartDesign::Fillet] Fillet007
  Base = -> Pocket008 [Edge208,Edge198,Edge218,Edge194]
  BaseFeature = -> Pocket008
  Radius = 3
  SupportTransform = false
  UseAllEdges = false
FEATURE [Sketcher::SketchObject] Sketch015
  ExternalGeometry = -> [Pocket005]
  FullyConstrained = true
  MapMode = 5
  Placement = pos=(0,53.625,0) rot=(0,0.707107,0.707107;3.14159rad)
  Support = -> [Pocket005]
  sketch-geometry (14):
    g0: GeomPoint X=1.6e-15 Y=3.25 Z=0
    g1: LineSegment StartX=6.5 StartY=1.25 StartZ=0 EndX=6.5 EndY=5.25 EndZ=0
    g2: LineSegment StartX=4.5 StartY=7.25 StartZ=0 EndX=-4.5 EndY=7.25 EndZ=0
    g3: LineSegment StartX=-6.5 StartY=5.25 StartZ=0 EndX=-6.5 EndY=1.25 EndZ=0
    g4: LineSegment StartX=-4.5 StartY=-0.75 StartZ=0 EndX=4.5 EndY=-0.75 EndZ=0
    g5: GeomPoint X=1.6e-15 Y=3.25 Z=0
    g6: ArcOfCircle CenterX=-4.5 CenterY=5.25 CenterZ=0 NormalX=0 NormalY=0 NormalZ=1 AngleXU=0 Radius=2 StartAngle=1.5708 EndAngle=3.14159
    g7: GeomPoint X=-6.5 Y=7.25 Z=0
    g8: ArcOfCircle CenterX=4.5 CenterY=5.25 CenterZ=0 NormalX=0 NormalY=0 NormalZ=1 AngleXU=0 Radius=2 StartAngle=0 EndAngle=1.5708
    g9: GeomPoint X=6.5 Y=7.25 Z=0
    g10: ArcOfCircle CenterX=4.5 CenterY=1.25 CenterZ=0 NormalX=0 NormalY=0 NormalZ=1 AngleXU=0 Radius=2 StartAngle=4.71239 EndAngle=6.28319
    g11: GeomPoint X=6.5 Y=-0.75 Z=0
    g12: ArcOfCircle CenterX=-4.5 CenterY=1.25 CenterZ=0 NormalX=0 NormalY=0 NormalZ=1 AngleXU=0 Radius=2 StartAngle=3.14159 EndAngle=4.71239
    g13: GeomPoint X=-6.5 Y=-0.75 Z=0
  constraints (29):
    c: Horizontal(g2)
    c: Horizontal(g4)
    c: Vertical(g1)
    c: Vertical(g3)
    c: Symmetric(g7,g11,g5)
    c: Coincident(g5,g0)
    c: DistanceX(g7,g9) = 13
    c: DistanceY(g13,g7) = 8
    c: PointOnObject(g7,g3)
    c: PointOnObject(g7,g2)
    c: Tangent(g3,g6) = -1.5708
    c: Tangent(g2,g6) = -1.5708
    c: Radius(g6) = 2
    c: PointOnObject(g9,g2)
    c: PointOnObject(g9,g1)
    c: Tangent(g2,g8) = -1.5708
    c: Tangent(g1,g8) = -1.5708
    c: PointOnObject(g11,g1)
    c: PointOnObject(g11,g4)
    c: Tangent(g1,g10) = -1.5708
    c: Tangent(g4,g10) = -1.5708
    c: PointOnObject(g13,g4)
    c: PointOnObject(g13,g3)
    c: Tangent(g4,g12) = -1.5708
    c: Tangent(g3,g12) = -1.5708
    c: Equal(g6,g12)
    c: Equal(g6,g8)
    c: Equal(g6,g10)
    c: Symmetric(g-4,g-3,g0)
FEATURE [PartDesign::Pocket] Pocket009  label="Pocket009 - USB"
  BaseFeature = -> Pocket005
  Direction = (0,-1,2e-16)
  Length = 2.5
  Length2 = 5
  Profile = -> Sketch015
  ReferenceAxis = -> Sketch015 [N_Axis]
  Type = 0
FEATURE [PartDesign::Chamfer] Chamfer
  Angle = 45
  Base = -> Fillet007 [Edge79,Edge85,Edge69,Edge192,Edge71,Edge86,Edge195,Edge77,Edge81,Edge84,Edge76,Edge75,Edge65,Edge198,Edge60,Edge189,Edge59,Edge63,Edge61,Edge70]
  BaseFeature = -> Fillet007
  ChamferType = 0
  FlipDirection = false
  Size = 0.5
  Size2 = 1
  SupportTransform = false
  UseAllEdges = false
FEATURE [PartDesign::Chamfer] Chamfer004  label="Chamfer004 - Thread"
  Angle = 45
  Base = -> Chamfer [Edge194,Edge107,Edge196,Edge91,Edge220,Face4,Edge163,Edge143,Edge131,Edge111,Edge133,Edge153,Edge165,Edge185,Edge175,Edge189,Edge288]
  BaseFeature = -> Chamfer
  ChamferType = 0
  FlipDirection = false
  Size = 0.2
  Size2 = 1
  SupportTransform = false
  UseAllEdges = false
FEATURE [Sketcher::SketchObject] Sketch010
  ExternalGeometry = -> [Pocket005]
  FullyConstrained = true
  MapMode = 5
  Placement = pos=(0,0,13.4) rot=(0,0,1;0rad)
  Support = -> [Pocket009]
  sketch-geometry (4):
    g0: Circle CenterX=-145.875 CenterY=50.625 CenterZ=0 NormalX=0 NormalY=0 NormalZ=1 AngleXU=0 Radius=0.8
    g1: Circle CenterX=145.875 CenterY=50.625 CenterZ=0 NormalX=0 NormalY=0 NormalZ=1 AngleXU=0 Radius=0.8
    g2: Circle CenterX=-145.875 CenterY=-50.625 CenterZ=0 NormalX=0 NormalY=0 NormalZ=1 AngleXU=0 Radius=0.8
    g3: Circle CenterX=145.875 CenterY=-50.625 CenterZ=0 NormalX=0 NormalY=0 NormalZ=1 AngleXU=0 Radius=0.8
  constraints (12):
    c: Diameter(g0) = 1.6
    c: DistanceY(g0,g-3) = 3
    c: DistanceX(g-3,g0) = 3
    c: Equal(g0,g1)
    c: Horizontal(g0,g1)
    c: DistanceX(g1,g-3) = 3
    c: Equal(g0,g2)
    c: Vertical(g0,g2)
    c: DistanceY(g-4,g2) = 3
    c: Horizontal(g2,g3)
    c: Vertical(g3,g1)
    c: Equal(g3,g0)
FEATURE [PartDesign::Hole] Hole001  label="Hole001 - Top frame screw"
  BaseFeature = -> Pocket009
  CustomThreadClearance = 0
  Depth = 6
  DepthType = 0
  Diameter = 1.6
  DrillForDepth = false
  DrillPoint = 1
  DrillPointAngle = 118
  HoleCutCountersinkAngle = 90
  HoleCutCustomValues = false
  HoleCutDepth = 0
  HoleCutDiameter = 6.1
  HoleCutType = 0
  ModelThread = false
  Profile = -> Sketch010
  Tapered = false
  TaperedAngle = 90
  ThreadClass = 0
  ThreadDepth = 6
  ThreadDepthType = 0
  ThreadDirection = 0
  ThreadFit = 0
  ThreadSize = 6
  ThreadType = 1
  Threaded = true
  UseCustomThreadClearance = false
FEATURE [PartDesign::Fillet] Fillet008
  Base = -> Hole001 [Edge276,Edge266,Edge278,Edge265]
  BaseFeature = -> Hole001
  Radius = 3
  SupportTransform = false
  UseAllEdges = false
FEATURE [Sketcher::SketchObject] Sketch016
  AttachmentOffset = pos=(0,0,-1.4) rot=(0,0,1;0rad)
  FullyConstrained = true
  MapMode = 5
  Placement = pos=(0,0,-1.4) rot=(0,0,1;0rad)
  Support = -> [XY_Plane004]
  sketch-geometry (8):
    g0: LineSegment StartX=120 StartY=48.4 StartZ=0 EndX=120 EndY=8.4 EndZ=0
    g1: LineSegment StartX=120 StartY=8.4 StartZ=0 EndX=-120 EndY=8.4 EndZ=0
    g2: LineSegment StartX=-120 StartY=8.4 StartZ=0 EndX=-120 EndY=48.4 EndZ=0
    g3: LineSegment StartX=-120 StartY=48.4 StartZ=0 EndX=-15 EndY=48.4 EndZ=0
    g4: LineSegment StartX=-15 StartY=48.4 StartZ=0 EndX=-15 EndY=18.4 EndZ=0
    g5: LineSegment StartX=-15 StartY=18.4 StartZ=0 EndX=15 EndY=18.4 EndZ=0
    g6: LineSegment StartX=15 StartY=18.4 StartZ=0 EndX=15 EndY=48.4 EndZ=0
    g7: LineSegment StartX=15 StartY=48.4 StartZ=0 EndX=120 EndY=48.4 EndZ=0
  constraints (24):
    c: Coincident(g7,g0)
    c: Coincident(g0,g1)
    c: Coincident(g1,g2)
    c: Coincident(g2,g3)
    c: Horizontal(g1)
    c: Vertical(g0)
    c: Vertical(g2)
    c: DistanceX(g1,g1) = 240
    c: DistanceY(g2,g2) = 40
    c: DistanceX(g1,g-1) = 120
    c: Coincident(g3,g4)
    c: Horizontal(g3)
    c: Coincident(g4,g5)
    c: Coincident(g5,g6)
    c: Horizontal(g5)
    c: Coincident(g6,g7)
    c: Horizontal(g7)
    c: Vertical(g6)
    c: Vertical(g4)
    c: DistanceY(g4,g4) = 30
    c: Equal(g4,g6)
    c: DistanceX(g5,g5) = 30
    c: DistanceX(g4,g-1) = 15
    c: DistanceY(g-1,g1) = 8.4
FEATURE [PartDesign::Pad] Pad004
  Direction = (0,0,1)
  Length = 3
  Length2 = 10
  Profile = -> Sketch016
  ReferenceAxis = -> Sketch016 [N_Axis]
  Type = 0
FEATURE [PartDesign::Fillet] Fillet009
  Base = -> Pad004 [Edge8,Edge5,Edge2,Edge1,Edge20,Edge11,Edge14,Edge17]
  BaseFeature = -> Pad004
  Radius = 2
  SupportTransform = false
  UseAllEdges = false
FEATURE [PartDesign::Chamfer] Chamfer005
  Angle = 45
  Base = -> Fillet008 [Edge68]
  BaseFeature = -> Fillet008
  ChamferType = 0
  FlipDirection = false
  Size = 1
  Size2 = 1
  SupportTransform = false
  UseAllEdges = false
FEATURE [Sketcher::SketchObject] Sketch017
  ExternalGeometry = -> [Chamfer005]
  FullyConstrained = true
  MapMode = 5
  Placement = pos=(0,-0.313585,-2.98357) rot=(1,0,0;3.03687rad)
  Support = -> [Chamfer005]
  sketch-geometry (4):
    g0: Circle CenterX=133.875 CenterY=38.7096 CenterZ=0 NormalX=0 NormalY=0 NormalZ=1 AngleXU=0 Radius=5
    g1: Circle CenterX=-133.875 CenterY=38.7096 CenterZ=0 NormalX=0 NormalY=0 NormalZ=1 AngleXU=0 Radius=5
    g2: Circle CenterX=133.875 CenterY=-39.1312 CenterZ=0 NormalX=0 NormalY=0 NormalZ=1 AngleXU=0 Radius=5
    g3: Circle CenterX=-133.875 CenterY=-39.1312 CenterZ=0 NormalX=0 NormalY=0 NormalZ=1 AngleXU=0 Radius=5
  constraints (12):
    c: Diameter(g0) = 10
    c: Equal(g0,g1)
    c: Horizontal(g0,g1)
    c: Equal(g2,g0)
    c: Vertical(g0,g2)
    c: Equal(g0,g3)
    c: Horizontal(g2,g3)
    c: Vertical(g1,g3)
    c: DistanceX(g-6,g1) = 15
    c: DistanceY(g1,g-3) = 15
    c: DistanceX(g0,g-4) = 15
    c: DistanceY(g-5,g2) = 15
FEATURE [PartDesign::Pocket] Pocket010
  BaseFeature = -> Chamfer005
  Direction = (0,0.104528,0.994522)
  Length = 1
  Length2 = 5
  Profile = -> Sketch017
  ReferenceAxis = -> Sketch017 [N_Axis]
  Type = 0
FEATURE [PartDesign::Chamfer] Chamfer006  label="Chamfer006 - Thread"
  Angle = 45
  Base = -> Pocket010 [Edge64,Edge48,Edge32,Edge39,Edge22,Edge188,Edge56,Edge189,Edge187,Edge59,Edge156,Edge158,Edge154,Edge47,Edge149,Edge151,Edge147,Edge31,Edge122,Edge121,Edge115,Edge131,Edge40,Edge130,Edge132,Edge11,Edge214,Edge97,Edge98,Edge95,Edge96]
  BaseFeature = -> Pocket010
  ChamferType = 0
  FlipDirection = false
  Size = 0.2
  Size2 = 1
  SupportTransform = false
  UseAllEdges = false
FEATURE [Sketcher::SketchObject] Sketch018
  ExternalGeometry = -> [Fillet009]
  FullyConstrained = true
  MapMode = 5
  Placement = pos=(0,0,1.6) rot=(0,0,1;0rad)
  Support = -> [Fillet009]
  sketch-geometry (2):
    g0: Circle CenterX=-110 CenterY=28.4 CenterZ=0 NormalX=0 NormalY=0 NormalZ=1 AngleXU=0 Radius=1.1
    g1: Circle CenterX=110 CenterY=28.4 CenterZ=0 NormalX=0 NormalY=0 NormalZ=1 AngleXU=0 Radius=1.1
  constraints (6):
    c: Diameter(g0) = 2.2
    c: DistanceX(g-3,g0) = 10
    c: DistanceY(g-4,g0) = 20
    c: Equal(g0,g1)
    c: Horizontal(g0,g1)
    c: DistanceX(g1,g-5) = 10
FEATURE [PartDesign::Hole] Hole002
  BaseFeature = -> Fillet009
  CustomThreadClearance = 0
  Depth = 20
  DepthType = 0
  Diameter = 2.2
  DrillForDepth = false
  DrillPoint = 1
  DrillPointAngle = 118
  HoleCutCountersinkAngle = 90
  HoleCutCustomValues = false
  HoleCutDepth = 0
  HoleCutDiameter = 4.4
  HoleCutType = 2
  ModelThread = false
  Profile = -> Sketch018
  Tapered = false
  TaperedAngle = 90
  ThreadClass = 0
  ThreadDepth = 20
  ThreadDepthType = 0
  ThreadDirection = 0
  ThreadFit = 1
  ThreadSize = 6
  ThreadType = 1
  Threaded = false
  UseCustomThreadClearance = false
FEATURE [PartDesign::Body] Body004  label="Weight"
  Group = -> [Sketch016,Pad004,Fillet009,Sketch018,Hole002]
  Origin = -> Origin004
  Tip = -> Hole002
FEATURE [Sketcher::SketchObject] Sketch019
  ExternalGeometry = -> [Chamfer006]
  FullyConstrained = true
  MapMode = 5
  Placement = pos=(0,0,-1.4) rot=(0,0,1;0rad)
  Support = -> [Chamfer006]
  sketch-geometry (2):
    g0: Circle CenterX=110 CenterY=28.425 CenterZ=0 NormalX=0 NormalY=0 NormalZ=1 AngleXU=0 Radius=0.8
    g1: Circle CenterX=-110 CenterY=28.425 CenterZ=0 NormalX=0 NormalY=0 NormalZ=1 AngleXU=0 Radius=0.8
  constraints (6):
    c: Diameter(g0) = 1.6
    c: Equal(g0,g1)
    c: Horizontal(g0,g1)
    c: DistanceX(g-3,g1) = 10.2
    c: DistanceY(g1,g-4) = 20.2
    c: DistanceX(g0,g-5) = 10.2
FEATURE [PartDesign::Hole] Hole003
  BaseFeature = -> Chamfer006
  CustomThreadClearance = 0
  Depth = 2.2
  DepthType = 0
  Diameter = 1.6
  DrillForDepth = false
  DrillPoint = 1
  DrillPointAngle = 118
  HoleCutCountersinkAngle = 90
  HoleCutCustomValues = false
  HoleCutDepth = 0
  HoleCutDiameter = 6.1
  HoleCutType = 0
  ModelThread = false
  Profile = -> Sketch019
  Tapered = false
  TaperedAngle = 90
  ThreadClass = 0
  ThreadDepth = 2.2
  ThreadDepthType = 0
  ThreadDirection = 0
  ThreadFit = 0
  ThreadSize = 6
  ThreadType = 1
  Threaded = true
  UseCustomThreadClearance = false
FEATURE [PartDesign::Body] Body001  label="Case"
  Group = -> [Sketch002,Pad001,Sketch003,Pocket001,Boolean,Fillet,Sketch006,Pocket003,Fillet001,Sketch007,Pocket004,Fillet003,Sketch008,Hole,Sketch009,Pocket005,Pocket009,Sketch010,Hole001,Sketch015,Fillet008,Chamfer005,Sketch017,Pocket010,Chamfer006,Sketch019,Hole003]
  Origin = -> Origin001
  Tip = -> Hole003
FEATURE [Sketcher::SketchObject] Sketch020
  AttachmentOffset = pos=(0,0,19.4) rot=(0,0,1;0rad)
  FullyConstrained = true
  MapMode = 5
  Placement = pos=(0,0,19.4) rot=(0,0,1;0rad)
  Support = -> [XY_Plane005]
  expr: .AttachmentOffset.Base.z = 19.4mm
  expr: Constraints[10] = 19.05mm * 3
  expr: Constraints[11] = 19.05mm
  expr: Constraints[20] = 3.5mm
  expr: Constraints[8] = 19.05mm * 4.5
  expr: Constraints[9] = 19.05mm * 1.5
  sketch-geometry (12):
    g0: LineSegment StartX=85.725 StartY=-28.575 StartZ=0 EndX=142.875 EndY=-28.575 EndZ=0
    g1: LineSegment StartX=142.875 StartY=-28.575 StartZ=0 EndX=142.875 EndY=-47.625 EndZ=0
    g2: LineSegment StartX=142.875 StartY=-47.625 StartZ=0 EndX=85.725 EndY=-47.625 EndZ=0
    g3: LineSegment StartX=85.725 StartY=-47.625 StartZ=0 EndX=85.725 EndY=-28.575 EndZ=0
    g4: LineSegment StartX=142.875 StartY=-47.625 StartZ=0 EndX=142.875 EndY=-32.075 EndZ=0
    g5: LineSegment StartX=142.875 StartY=-32.075 StartZ=0 EndX=89.225 EndY=-32.075 EndZ=0
    g6: LineSegment StartX=89.225 StartY=-32.075 StartZ=0 EndX=89.225 EndY=-47.625 EndZ=0
    g7: LineSegment StartX=89.225 StartY=-47.625 StartZ=0 EndX=142.875 EndY=-47.625 EndZ=0
    g8: ArcOfCircle CenterX=97 CenterY=-39.85 CenterZ=0 NormalX=0 NormalY=0 NormalZ=1 AngleXU=0 Radius=7.775 StartAngle=1.5708 EndAngle=4.71239
    g9: ArcOfCircle CenterX=135.1 CenterY=-39.85 CenterZ=0 NormalX=0 NormalY=0 NormalZ=1 AngleXU=0 Radius=7.775 StartAngle=4.71239 EndAngle=7.85398
    g10: LineSegment StartX=97 StartY=-47.625 StartZ=0 EndX=135.1 EndY=-47.625 EndZ=0
    g11: LineSegment StartX=135.1 StartY=-32.075 StartZ=0 EndX=97 EndY=-32.075 EndZ=0
  constraints (33):
    c: Coincident(g0,g1)
    c: Coincident(g1,g2)
    c: Coincident(g2,g3)
    c: Coincident(g3,g0)
    c: Horizontal(g0)
    c: Horizontal(g2)
    c: Vertical(g1)
    c: Vertical(g3)
    c: DistanceX(g-1,g0) = 85.725
    c: DistanceY(g0,g-1) = 28.575
    c: DistanceX(g2,g2) = 57.15
    c: DistanceY(g1,g1) = 19.05
    c: Coincident(g4,g5)
    c: Coincident(g5,g6)
    c: Coincident(g6,g7)
    c: Coincident(g7,g4)
    c: Horizontal(g5)
    c: Horizontal(g7)
    c: Vertical(g4)
    c: Vertical(g6)
    c: DistanceY(g5,g0) = 3.5
    c: DistanceX(g0,g5) = 3.5
    c: Coincident(g4,g1)
    c: Tangent(g8,g10) = -1.5708
    c: Tangent(g10,g9) = -1.5708
    c: Tangent(g9,g11) = -1.5708
    c: Tangent(g11,g8) = -1.5708
    c: Equal(g8,g9)
    c: Horizontal(g10)
    c: PointOnObject(g8,g5)
    c: PointOnObject(g8,g2)
    c: Tangent(g9,g1)
    c: Tangent(g6,g8)
FEATURE [PartDesign::Pad] Pad005
  Direction = (0,0,1)
  Length = 3
  Length2 = 3
  Profile = -> Sketch020
  ReferenceAxis = -> Sketch020 [N_Axis]
  Type = 4
FEATURE [PartDesign::Fillet] Fillet011
  Base = -> Pad005 [Face5]
  BaseFeature = -> Pad005
  Radius = 3
  SupportTransform = false
  UseAllEdges = false
FEATURE [PartDesign::Body] Body005
  Group = -> [Sketch020,Pad005,Fillet011]
  Origin = -> Origin005
  Tip = -> Fillet011
FEATURE [PartDesign::Boolean] Boolean001
  BaseFeature = -> Chamfer004
  Group = -> [Body005]
  Type = 1
FEATURE [PartDesign::Chamfer] Chamfer007
  Angle = 45
  Base = -> Boolean001 [Edge135]
  BaseFeature = -> Boolean001
  ChamferType = 0
  FlipDirection = false
  Size = 0.5
  Size2 = 1
  SupportTransform = false
  UseAllEdges = false
FEATURE [PartDesign::Body] Body003  label="Top Frame"
  Group = -> [Sketch011,Pad003,Sketch012,Pocket006,Fillet005,Fillet006,Sketch013,Pocket007,Sketch014,Pocket008,Fillet007,Chamfer,Chamfer004,Boolean001,Chamfer007]
  Origin = -> Origin003
  Tip = -> Chamfer007
FEATURE [TechDraw::DrawSVGTemplate] Template
  Height = 297
  Orientation = 1
  Width = 420
FEATURE [TechDraw::DrawViewPart] View
  CoarseView = false
  Direction = (0,0,1)
  Focus = 100
  HardHidden = false
  IsoCount = 0
  IsoHidden = false
  IsoVisible = false
  LockPosition = false
  Perspective = false
  Rotation = 0
  ScaleType = 0
  SeamHidden = false
  SeamVisible = true
  SmoothHidden = false
  SmoothVisible = true
  Source = -> [Body001]
  X = 209.897
  XDirection = (1,0,0)
  Y = 148.448
FEATURE [TechDraw::DrawViewBalloon] Balloon
  BubbleShape = 1
  EndType = 0
  EndTypeScale = 1
  KinkLength = 5
  LockPosition = false
  OriginX = -146.675
  OriginY = 50.6271
  Rotation = 0
  ScaleType = 0
  ShapeScale = 1
  SourceView = -> View
  Text = M2 x 6mm
  TextWrapLen = -1
  X = -119.649
  Y = 69.3191
FEATURE [TechDraw::DrawViewBalloon] Balloon001
  BubbleShape = 1
  EndType = 0
  EndTypeScale = 1
  KinkLength = 5
  LockPosition = false
  OriginX = -146.675
  OriginY = -50.6229
  Rotation = 0
  ScaleType = 0
  ShapeScale = 1
  SourceView = -> View
  Text = M2 x 6mm
  TextWrapLen = -1
  X = -117.369
  Y = -36.085
FEATURE [TechDraw::DrawViewBalloon] Balloon002
  BubbleShape = 1
  EndType = 0
  EndTypeScale = 1
  KinkLength = 5
  LockPosition = false
  OriginX = 145.075
  OriginY = 50.6271
  Rotation = 0
  ScaleType = 0
  ShapeScale = 1
  SourceView = -> View
  Text = M2 x 6mm
  TextWrapLen = -1
  X = 108.094
  Y = 69.7081
FEATURE [TechDraw::DrawViewBalloon] Balloon003
  BubbleShape = 1
  EndType = 0
  EndTypeScale = 1
  KinkLength = 5
  LockPosition = false
  OriginX = 145.075
  OriginY = -50.6229
  Rotation = 0
  ScaleType = 0
  ShapeScale = 1
  SourceView = -> View
  Text = M2 x 6mm
  TextWrapLen = -1
  X = 111.31
  Y = -33.8396
FEATURE [TechDraw::DrawViewBalloon] Balloon004
  BubbleShape = 1
  EndType = 0
  EndTypeScale = 1
  KinkLength = 5
  LockPosition = false
  OriginX = -12.7997
  OriginY = 46.3396
  Rotation = 0
  ScaleType = 0
  ShapeScale = 1
  SourceView = -> View
  Text = M2 x 2.6mm
  TextWrapLen = -1
  X = -38.6547
  Y = 36.6688
FEATURE [TechDraw::DrawViewBalloon] Balloon005
  BubbleShape = 1
  EndType = 0
  EndTypeScale = 1
  KinkLength = 5
  LockPosition = false
  OriginX = 11.2003
  OriginY = 46.3396
  Rotation = 0
  ScaleType = 0
  ShapeScale = 1
  SourceView = -> View
  Text = M2 x 2.6mm
  TextWrapLen = -1
  X = 37.2693
  Y = 36.5002
FEATURE [TechDraw::DrawViewBalloon] Balloon006
  BubbleShape = 1
  EndType = 0
  EndTypeScale = 1
  KinkLength = 5
  LockPosition = false
  OriginX = -12.7997
  OriginY = 22.3396
  Rotation = 0
  ScaleType = 0
  ShapeScale = 1
  SourceView = -> View
  Text = M2 x 2.6mm
  TextWrapLen = -1
  X = -38.6547
  Y = 28.3472
FEATURE [TechDraw::DrawViewBalloon] Balloon007
  BubbleShape = 1
  EndType = 0
  EndTypeScale = 1
  KinkLength = 5
  LockPosition = false
  OriginX = 11.2003
  OriginY = 22.3396
  Rotation = 0
  ScaleType = 0
  ShapeScale = 1
  SourceView = -> View
  Text = M2 x 2.6mm
  TextWrapLen = -1
  X = 37.6065
  Y = 29.6958
FEATURE [TechDraw::DrawViewBalloon] Balloon008
  BubbleShape = 1
  EndType = 0
  EndTypeScale = 1
  KinkLength = 5
  LockPosition = false
  OriginX = -110.8
  OriginY = 28.4271
  Rotation = 0
  ScaleType = 0
  ShapeScale = 1
  SourceView = -> View
  Text = M2 x 2.2mm
  TextWrapLen = -1
  X = -85.2595
  Y = 38.7317
FEATURE [TechDraw::DrawViewBalloon] Balloon009
  BubbleShape = 1
  EndType = 0
  EndTypeScale = 1
  KinkLength = 5
  LockPosition = false
  OriginX = 109.2
  OriginY = 28.4271
  Rotation = 0
  ScaleType = 0
  ShapeScale = 1
  SourceView = -> View
  Text = M2 x 2.2mm
  TextWrapLen = -1
  X = 81.8618
  Y = 19.053
FEATURE [TechDraw::DrawPage] Page  label="Case - TechDraw"
  KeepUpdated = true
  NextBalloonIndex = 11
  ProjectionType = 0
  Template = -> Template
  Views = -> [View,Balloon,Balloon001,Balloon002,Balloon003,Balloon004,Balloon005,Balloon006,Balloon007,Balloon008,Balloon009]
